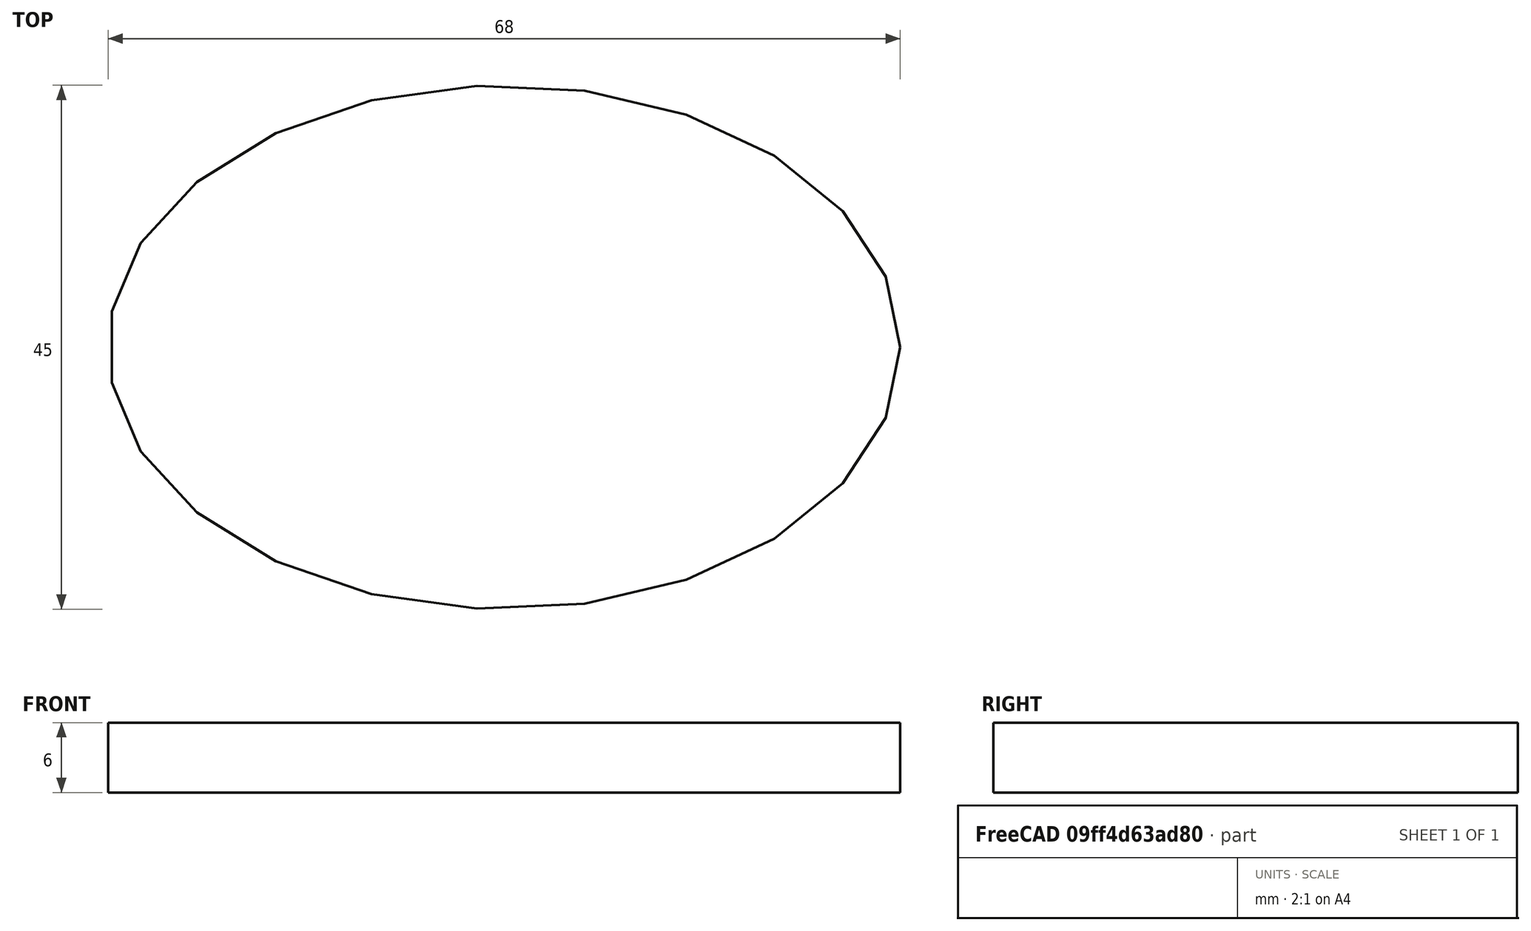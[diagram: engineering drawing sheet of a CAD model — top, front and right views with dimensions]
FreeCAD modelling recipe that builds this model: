
FCSTD DOCUMENT  (FreeCAD 0.17R13541 (Git))
Label: Digi-Night-Light-8Dense-LEDS-Oval-USB-V0.11
License: All rights reserved
LicenseURL: http://en.wikipedia.org/wiki/All_rights_reserved
objects: Sketcher::SketchObject×2, PartDesign::Pad×1, PartDesign::Body×1, App::Part×1
note: 5 computed .brp shape members not serialized (recipe doc carries the construction recipe); baked Part::Feature solids carry a one-line shape summary decoded from their .brp

FEATURE [Sketcher::SketchObject] Sketch
  MapMode = 5
  Support = -> [XY_Plane001]
  sketch-geometry (6):
    g0: Ellipse CenterX=0 CenterY=0 CenterZ=0 NormalX=0 NormalY=0 NormalZ=1 MajorRadius=34 MinorRadius=22.5 AngleXU=0
    g1: LineSegment [constr] StartX=34 StartY=0 StartZ=0 EndX=-34 EndY=0 EndZ=0
    g2: LineSegment [constr] StartX=0 StartY=22.5 StartZ=0 EndX=0 EndY=-22.5 EndZ=0
    g3: GeomPoint X=25.4902 Y=0 Z=0
    g4: GeomPoint X=-25.4902 Y=0 Z=0
    g5: LineSegment StartX=-6.25 StartY=-22.1166 StartZ=0 EndX=6.25 EndY=-22.1166 EndZ=0
  constraints (9):
    c: InternalAlignment(g1-g4 -> g0) x4
    c: Coincident(g0,g-1)
    c: PointOnObject(g2,g-2)
    c: Distance(g2,g2) = 45
    c: Distance(g1,g1) = 68
    c: PointOnObject(g5,g0)
    c: PointOnObject(g5,g0)
    c: Horizontal(g5)
    c: Distance(g5,g5) = 12.5
FEATURE [PartDesign::Pad] Pad
  Length = 6
  Length2 = 100
  Profile = -> Sketch
  Type = 0
FEATURE [Sketcher::SketchObject] Sketch001
  ExternalGeometry = -> [Pad]
  MapMode = 5
  Placement = pos=(0,0,0) rot=(1,0,0;3.14159rad)
  Support = -> [Pad]
  sketch-geometry (9):
    g0: LineSegment StartX=9.775 StartY=-3.45006 StartZ=0 EndX=9.775 EndY=-21.5501 EndZ=0
    g1: LineSegment StartX=9.775 StartY=-21.5501 StartZ=0 EndX=-9.775 EndY=-21.5501 EndZ=0
    g2: LineSegment StartX=-9.775 StartY=-21.5501 StartZ=0 EndX=-9.775 EndY=-3.45006 EndZ=0
    g3: LineSegment StartX=-28.5 StartY=8.54994 StartZ=0 EndX=28.5 EndY=8.54994 EndZ=0
    g4: LineSegment StartX=28.5 StartY=8.54994 StartZ=0 EndX=28.5 EndY=-3.45006 EndZ=0
    g5: LineSegment StartX=-28.5 StartY=-3.45006 StartZ=0 EndX=-28.5 EndY=8.54994 EndZ=0
    g6: GeomPoint X=0 Y=8.54994 Z=0
    g7: LineSegment StartX=-28.5 StartY=-3.45006 StartZ=0 EndX=-9.775 EndY=-3.45006 EndZ=0
    g8: LineSegment StartX=9.775 StartY=-3.45006 StartZ=0 EndX=28.5 EndY=-3.45006 EndZ=0
  constraints (26):
    c: Coincident(g0,g1)
    c: Coincident(g1,g2)
    c: Horizontal(g1)
    c: Vertical(g0)
    c: Vertical(g2)
    c: PointOnObject(g1,g-3)
    c: PointOnObject(g0,g-3)
    c: Distance(g1) = 19.55
    c: Distance(g0) = 18.1
    c: Coincident(g3,g4)
    c: Coincident(g5,g3)
    c: Horizontal(g3)
    c: Vertical(g4)
    c: Vertical(g5)
    c: Distance(g4) = 12
    c: Distance(g3) = 57
    c: PointOnObject(g6,g3)
    c: Symmetric(g3,g3,g6)
    c: PointOnObject(g6,g-2)
    c: Coincident(g7,g5)
    c: Coincident(g7,g2)
    c: Horizontal(g7)
    c: Coincident(g8,g0)
    c: Coincident(g8,g4)
    c: Horizontal(g8)
    c: Distance(g2) = 18.1
FEATURE [PartDesign::Body] Body
  Group = -> [Sketch,Pad,Sketch001]
  Origin = -> Origin001
  Tip = -> Pad
FEATURE [App::Part] Part
  Group = -> [Body]
  License = CC BY 3.0
  LicenseURL = http://creativecommons.org/licenses/by/3.0/
  Origin = -> Origin
